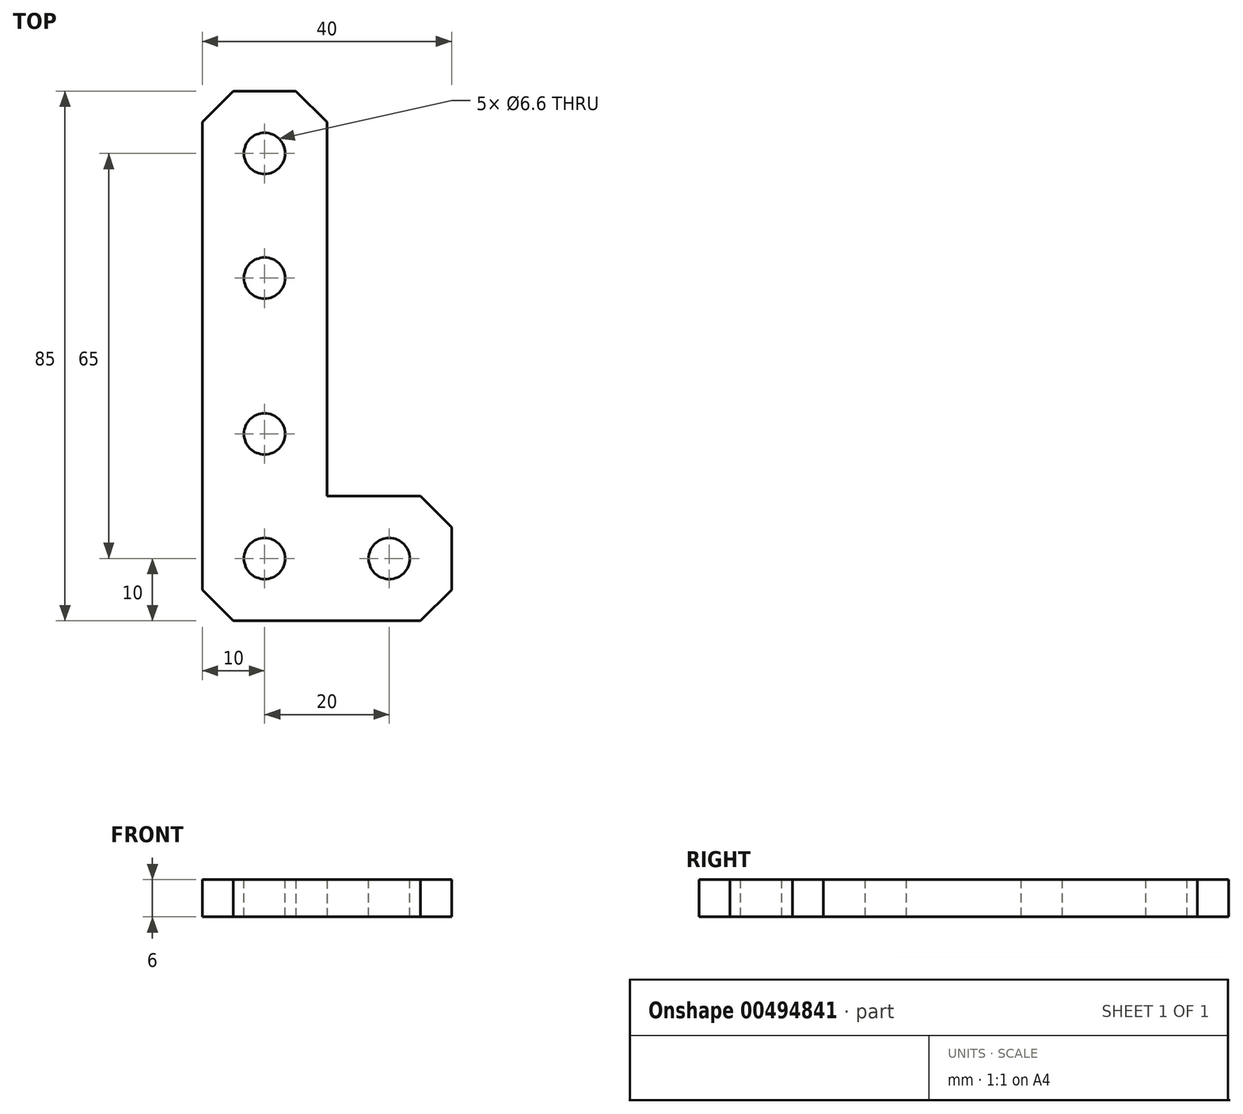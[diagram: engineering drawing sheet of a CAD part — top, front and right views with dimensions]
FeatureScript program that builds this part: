
annotation { "Feature Type Name" : "Feature", "Feature Type Description" : "" }
export const myFeature = defineFeature(function(context is Context, id is Id, definition is map)
    precondition{}
    {
        {
            var Q0;
            Q0=qCreatedBy(makeId("Top.planeOp"),FACE);
            var sketch = newSketch(context, id + "F0", { "sketchPlane" : qUnion([Q0])});
            skLineSegment(sketch, "E0.bottom", {"start": v(0, 0) * mm, "end": v(20, 0) * mm});
            skLineSegment(sketch, "E0.top", {"start": v(0, 85) * mm, "end": v(20, 85) * mm});
            skLineSegment(sketch, "E0.left", {"start": v(0, 0) * mm, "end": v(0, 85) * mm});
            skLineSegment(sketch, "E0.right", {"start": v(20, 20) * mm, "end": v(20, 85) * mm});
            skLineSegment(sketch, "E1.bottom", {"start": v(20, 20) * mm, "end": v(40, 20) * mm});
            skLineSegment(sketch, "E1.top", {"start": v(15.61, 0) * mm, "end": v(40, 0) * mm});
            skLineSegment(sketch, "E1.right", {"start": v(40, 20) * mm, "end": v(40, 0) * mm});
            skSolve(sketch);
        }
        {
            var Q0;
            Q0=qSketchRegion(id+"F0",true);
            extrude(context, id + "F1", {"entities" : qUnion([Q0]), "depth" : 6 * mm});
        }
        {
            var Q0;
            Q0=makeQuery(id+"F1.opExtrude","CAP_FACE",FACE,{"disambiguationData":[OSD([sQuery(id+"F0.wireOp",EDGE,"E0.bottom"),sQuery(id+"F0.wireOp",EDGE,"E0.top"),sQuery(id+"F0.wireOp",EDGE,"E0.left"),sQuery(id+"F0.wireOp",EDGE,"E0.right"),sQuery(id+"F0.wireOp",EDGE,"E1.bottom"),sQuery(id+"F0.wireOp",EDGE,"E1.top"),sQuery(id+"F0.wireOp",EDGE,"E1.right")])],"isStart":false});
            var sketch = newSketch(context, id + "F2", { "sketchPlane" : qUnion([Q0])});
            skPoint(sketch, "E2", {"position": v(10, 75) * mm});
            skPoint(sketch, "E3", {"position": v(10, 55) * mm});
            skPoint(sketch, "E4", {"position": v(10, 10) * mm});
            skPoint(sketch, "E5", {"position": v(30, 10) * mm});
            skPoint(sketch, "E6", {"position": v(10, 30) * mm});
            skSolve(sketch);
        }
        {
            var Q0;
            Q0=sQuery(id+"F2.wireOp",VERTEX,"E2");
            var Q1;
            Q1=sQuery(id+"F2.wireOp",VERTEX,"E3");
            var Q2;
            Q2=sQuery(id+"F2.wireOp",VERTEX,"E4");
            var Q3;
            Q3=sQuery(id+"F2.wireOp",VERTEX,"E5");
            var Q4;
            Q4=sQuery(id+"F2.wireOp",VERTEX,"E6");
            var Q5;
            Q5=makeQuery(id+"F1.opExtrude","SWEPT_BODY",BODY,{"disambiguationData":[OSD([sQuery(id+"F0.wireOp",EDGE,"E0.bottom"),sQuery(id+"F0.wireOp",EDGE,"E0.top"),sQuery(id+"F0.wireOp",EDGE,"E0.left"),sQuery(id+"F0.wireOp",EDGE,"E0.right"),sQuery(id+"F0.wireOp",EDGE,"E1.bottom"),sQuery(id+"F0.wireOp",EDGE,"E1.top"),sQuery(id+"F0.wireOp",EDGE,"E1.right")])]});
            hole(context, id + "F3", {"style" : HoleStyle.SIMPLE, "endStyle" : HoleEndStyle.THROUGH, "standardTappedOrClearance" : lookupTablePath({ "standard" : "ISO", "fit" : "Normal", "size" : "M6", "type" : "Clearance" }), "standardBlindInLast" : lookupTablePath({ "fit" : "Standard", "standard" : "ISO", "size" : "M6", "type" : "Clearance" }), "holeDiameter" : 6.6 * mm, "isTappedThrough" : true, "tappedDepth" : 7.6 * mm, "tapClearance" : 3, "locations" : qUnion([Q0, Q1, Q2, Q3, Q4]), "scope" : qUnion([Q5])});
        }
        {
            var Q0;
            Q0=makeQuery(id+"F1.opExtrude","SWEPT_EDGE",EDGE,{"disambiguationData":[OSD([sQuery(id+"F0.wireOp",EDGE,"E0.top"),sQuery(id+"F0.wireOp",EDGE,"E0.right")])]});
            var Q1;
            Q1=makeQuery(id+"F1.opExtrude","SWEPT_EDGE",EDGE,{"disambiguationData":[OSD([sQuery(id+"F0.wireOp",EDGE,"E0.top"),sQuery(id+"F0.wireOp",EDGE,"E0.left")])]});
            var Q2;
            Q2=makeQuery(id+"F1.opExtrude","SWEPT_EDGE",EDGE,{"disambiguationData":[OSD([sQuery(id+"F0.wireOp",EDGE,"E1.bottom"),sQuery(id+"F0.wireOp",EDGE,"E1.right")])]});
            var Q3;
            Q3=makeQuery(id+"F1.opExtrude","SWEPT_EDGE",EDGE,{"disambiguationData":[OSD([sQuery(id+"F0.wireOp",EDGE,"E1.top"),sQuery(id+"F0.wireOp",EDGE,"E1.right")])]});
            var Q4;
            Q4=makeQuery(id+"F1.opExtrude","SWEPT_EDGE",EDGE,{"disambiguationData":[OSD([sQuery(id+"F0.wireOp",EDGE,"E0.bottom"),sQuery(id+"F0.wireOp",EDGE,"E0.left")])]});
            chamfer(context, id + "F4", {"entities" : qUnion([Q0, Q1, Q2, Q3, Q4]), "width" : 5 * mm, "tangentPropagation" : true});
        }
    });
